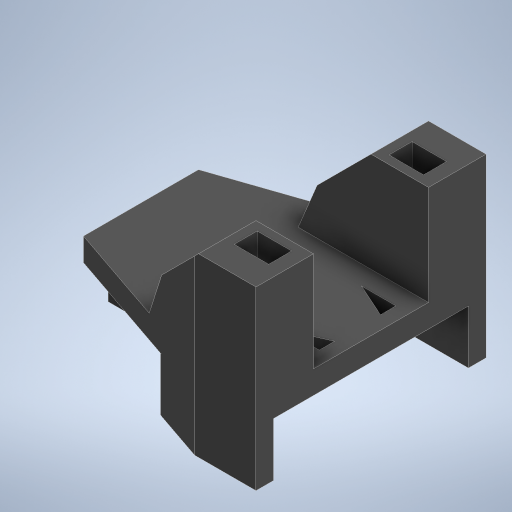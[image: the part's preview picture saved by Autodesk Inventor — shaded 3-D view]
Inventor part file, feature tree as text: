
AUTODESK INVENTOR PART (.ipt)
format: ipt  version: 2024.2 (Build 282272000, 272)  size: 375,808 bytes
history: native  units: mm
features: extrude x7, sketch x7, chamfer x2, fillet x1
ambient origin geometry x8: Origin, YZ Plane, XZ Plane, XY Plane, X Axis, Y Axis, Z Axis, Center Point
bodies: Solid1 (feature_tree)
feature tree (17):
  extrude  "Extrusion1"  Depth=2.3mm
  extrude  "Extrusion2"  Depth=7.0mm TaperAngle=0.0deg
  extrude  "Extrusion3"  Depth=3.0mm
  fillet  "Fillet1"  Radius=24.0mm
  extrude  "Extrusion4"  Depth=0.2mm
  extrude  "Extrusion5"  Depth=4.0mm
  extrude  "Extrusion7"  Depth=15.0mm
  chamfer  "Chamfer1"  Distance=4.0mm
  chamfer  "Chamfer2"  Distance=3.0mm
  extrude  "Extrusion10"  Depth=2.0mm
  sketch  "Sketch1"  dims[d0=30.0mm d1=8.0mm d2=4.5mm d3=3.0mm d4=3.0mm d5=17.2mm d6=3.4mm d7=1.75mm d8=15.0mm d9=7.5mm d10=22.0mm d11=22.0mm d12=3.0mm d13=0.0mm d14=2.3mm]
  sketch  "Sketch2"  dims[d15=2.3mm d24=7.0mm d25=0.0mm]
  sketch  "Sketch3"  dims[d26=14.746667mm d27=3.0mm d28=24.0mm]
  sketch  "Sketch4"  dims[d29=14.6mm d30=0.2mm]
  sketch  "Sketch5"  dims[d31=2.8mm d32=4.0mm]
  sketch  "Sketch6"  dims[d33=7.0mm d34=15.0mm d35=4.0mm d36=0.0mm]
  sketch  "Sketch9"  dims[d37=2.0mm d38=3.0mm d39=2.0mm d40=2.0mm d41=3.0mm d42=5.0mm d43=0.0mm d44=6.0mm d45=15.5mm d46=5.0mm d47=5.0mm d48=0.0mm d52=3.0mm d55=17.0mm d56=1.1mm d57=17.0mm d58=1.1mm d59=13.0mm d60=0.0mm d61=9.5mm d62=2.0mm d63=45.0deg d64=3.5mm d65=2.0mm d66=45.0deg d84=1.0mm d85=0.0mm d86=0.5mm d87=0.872665mm]
